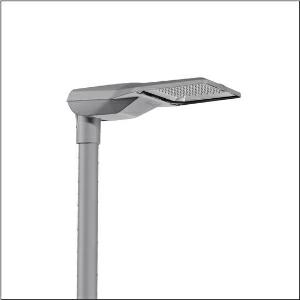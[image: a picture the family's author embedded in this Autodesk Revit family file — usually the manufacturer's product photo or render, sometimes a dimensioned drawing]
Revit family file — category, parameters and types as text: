
# Revit family: streetlight_sl_21_midi___pc-r_5xe7g43a08mb_b1b0
name_source: partatom
category: Lighting Fixtures
units: mm (PartAtom-declared; Revit-internal decimal feet)

## family parameters
Cut with Voids When Loaded = No
Host = Face
Light Source = No
Part Type = Normal
Room Calculation Point = No
Round Connector Dimension = Use Diameter
Shared = No

## types (1)
- --- (1 x LED, 19200 lm, 147 W, 4000K)
    Apparent Load = 147 VA
    CIE Flux Codes = 38 78 98 100 100
    Color Rendering = 70
    Color Temperature = 4000K
    Default Elevation = 1800 mm
    Description = Streetlight SL 21 midi, mast luminaire, primary light control with lens, of PMMA, primary optical cover: cover, of toughened safety glass, transparent, light distribution: PC-R, light emission: direct distribution, primary light characteristic: asymmetric, right, installation type: post-top, side-entry, LED, 3G 1.5mm², High Power LED, rated luminous flux: 19.200lm, luminous efficacy: 131lm/W, light colour: 740, colour temperature: 4000K, control: overheat protection, constant luminous flux control, time-dependent luminous flux control, flexible luminous flux parameterisation, mains connection: 220..240V, AC, 50/60Hz, connection cable pre-assembled, cable length: 12,5m, wiring characteristics: H07RN-F, start of lifetime: 147W, end of service life: 155W, reduction: 64W, luminaire housing, of diecast aluminium, powder-coated, Siteco® metallic grey (DB 702S), corrosivity category C5 mid according to DIN EN ISO 12944, please order mast flange separately, inclination adjustable: 0°, 5°, 10°, 15°, sealing non-destructively replaceable, multi-level sealing system, length: 644mm, width: 335mm, height: 110mm, mast flange for spigot size: 42mm (side-entry): 5XC10008XM4, 60/48mm (side-entry/post-top): 5XC10108XM2, 76/60mm (side-entry/post-top): 5XC10108XM1, protection rating (complete): IP66, insulation class (complete): insulation class II (safety insulation), certification: CE, ENEC, ENEC+, VDE, impact resistance: IK09, permissible operating ambient temperature for outdoor applications: -40..+50°C, standard-compliant lighting for roads and squares, packaging unit: 1 piece

Light Distribution: PC-R
    Height = 111 mm
    Lamp = 1 x LED
    Lamp Light Flux = 19200 lm
    Lamp Power = 147 W
    Lamp count = 1
    Length = 644 mm
    Luminous efficacy = 131 lm/W
    Manufacturer = Siteco
    ModVariant = No
    Model = 5XE7G43A08MB
    Number of Poles = 1
    OnlyDefault = Yes
    Power Factor = 1
    Product Name = Streetlight SL 21 midi | PC-R
    Product group = mast luminaire | pylon top
    ProductGroupID = 6100
    Protection Class = Protection class II
    Protection Degree = IP 66
    RLX_Detail_Level = 1
    RLX_Emergency_Light_Flux = 0 lm
    RLX_Emergency_Type = 0
    RLX_Emergency_Type_DB = No
    RlxData = <blob elided: 92841 chars, md5=e440747d>
    Socket = socket
    Standby Power = 0 W
    System Light Flux = 19200 lm
    System Power = 147 W
    Type Comments = factory setting: luminous flux: 100 % | Output Level: 100 % | 750 mA
    Type Image = l_1004298.jpg
    URL = http://relux.com
    VarID = @adj_022647
    Voltage = 0 V
    Weight = 0.00 kg
    Width = 336 mm

## geometry (parser evidence)
native form markers: Blend x4, Sweep x10
no freeform markers — native parametric forms only
